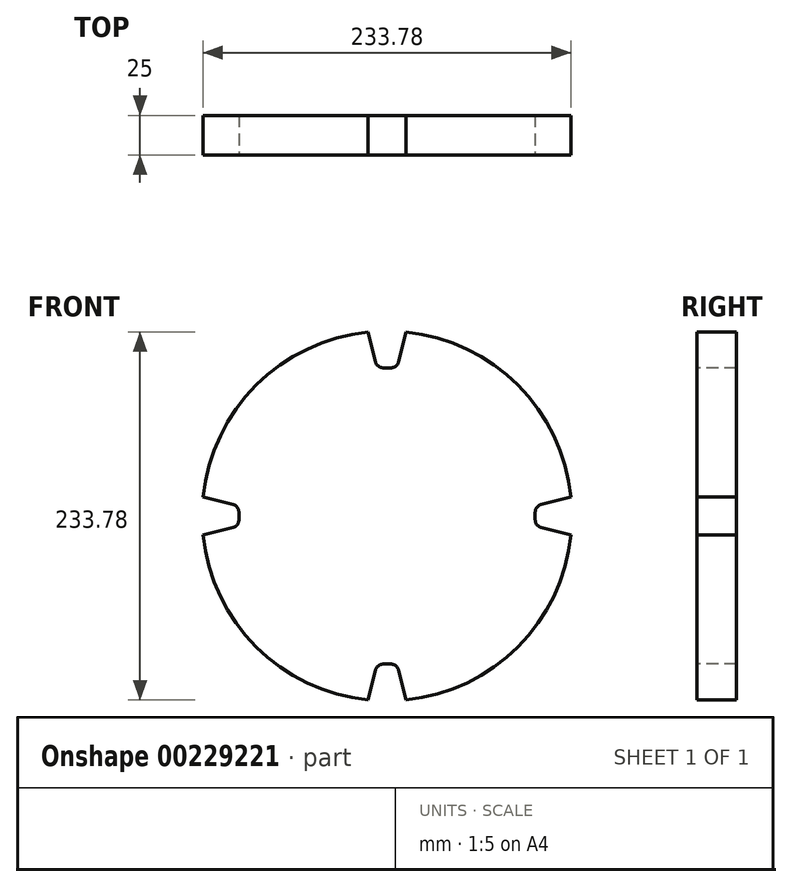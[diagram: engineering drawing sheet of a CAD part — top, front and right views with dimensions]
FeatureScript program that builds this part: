
annotation { "Feature Type Name" : "Feature", "Feature Type Description" : "" }
export const myFeature = defineFeature(function(context is Context, id is Id, definition is map)
    precondition{}
    {
        {
            var Q0;
            Q0=qCreatedBy(makeId("Front.planeOp"),FACE);
            var sketch = newSketch(context, id + "F0", { "sketchPlane" : qUnion([Q0])});
            skCircle(sketch, "E0", {"center": v(0, 0) * mm, "radius": 117.5 * mm});
            skSolve(sketch);
        }
        {
            var Q0;
            Q0 = qSketchRegion(id + "F0", true);
            extrude(context, id + "F1", {"entities" : qUnion([Q0]), "endBound" : BoundingType.SYMMETRIC, "depth" : 25 * mm});
        }
        {
            var Q0;
            Q0=qCreatedBy(makeId("Front.planeOp"),FACE);
            var sketch = newSketch(context, id + "F2", { "sketchPlane" : qUnion([Q0])});
            skArc(sketch, "E1.0", {"start": v(11.98, 116.89) * mm, "mid": v(0, 117.5) * mm, "end": v(-11.98, 116.89) * mm});
            skLineSegment(sketch, "E2", {"start": v(-11.98, 116.89) * mm, "end": v(-7.33, 97.9) * mm});
            skLineSegment(sketch, "E3", {"start": v(-2.47, 94.1) * mm, "end": v(2.47, 94.1) * mm});
            skLineSegment(sketch, "E4", {"start": v(7.33, 97.9) * mm, "end": v(11.98, 116.89) * mm});
            skPoint(sketch, "E5.visualSharp", {"position": v(-6.4, 94.1) * mm});
            skArc(sketch, "E5.filletArc", {"start": v(-7.33, 97.9) * mm, "mid": v(-5.56, 95.16) * mm, "end": v(-2.47, 94.1) * mm});
            skPoint(sketch, "E6.visualSharp", {"position": v(6.4, 94.1) * mm});
            skArc(sketch, "E6.filletArc", {"start": v(2.47, 94.1) * mm, "mid": v(5.56, 95.16) * mm, "end": v(7.33, 97.9) * mm});
            skSolve(sketch);
        }
        {
            var Q0;
            Q0 = qSketchRegion(id + "F2", true);
            extrude(context, id + "F3", {"entities" : qUnion([Q0]), "operationType" : NewBodyOperationType.REMOVE, "endBound" : BoundingType.SYMMETRIC, "oppositeDirection" : true, "depth" : 25 * mm});
        }
        {
            var Q0;
            Q0=makeQuery(id+"F3.boolean.opBoolean","COPY",FACE,{"derivedFrom":makeQuery(id+"F3.opExtrude","SWEPT_FACE",FACE,{"disambiguationData":[OSD([sQuery(id+"F2.wireOp",EDGE,"E4")])]})});
            var Q1;
            Q1=makeQuery(id+"F3.boolean.opBoolean","COPY",FACE,{"derivedFrom":makeQuery(id+"F3.opExtrude","SWEPT_FACE",FACE,{"disambiguationData":[OSD([sQuery(id+"F2.wireOp",EDGE,"E6.filletArc")])]})});
            var Q2;
            Q2=makeQuery(id+"F3.boolean.opBoolean","COPY",FACE,{"derivedFrom":makeQuery(id+"F3.opExtrude","SWEPT_FACE",FACE,{"disambiguationData":[OSD([sQuery(id+"F2.wireOp",EDGE,"E3")])]})});
            var Q3;
            Q3=makeQuery(id+"F3.boolean.opBoolean","COPY",FACE,{"derivedFrom":makeQuery(id+"F3.opExtrude","SWEPT_FACE",FACE,{"disambiguationData":[OSD([sQuery(id+"F2.wireOp",EDGE,"E5.filletArc")])]})});
            var Q4;
            Q4=makeQuery(id+"F3.boolean.opBoolean","COPY",FACE,{"derivedFrom":makeQuery(id+"F3.opExtrude","SWEPT_FACE",FACE,{"disambiguationData":[OSD([sQuery(id+"F2.wireOp",EDGE,"E2")])]})});
            var Q5;
            Q5=makeQuery(id+"F1.opExtrude","SWEPT_FACE",FACE,{"disambiguationData":[OSD([sQuery(id+"F0.wireOp",EDGE,"E0")])]});
            circularPattern(context, id + "F4", {"patternType" : PatternType.FACE, "faces" : qUnion([Q0, Q1, Q2, Q3, Q4]), "axis" : qUnion([Q5]), "angle" : 360 * degree, "instanceCount" : 4, "equalSpace" : true});
        }
    });
